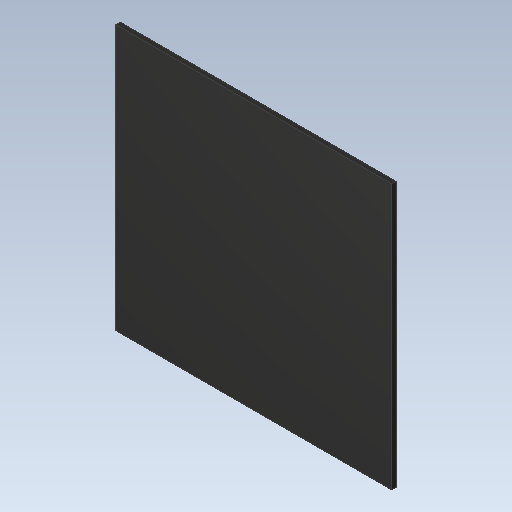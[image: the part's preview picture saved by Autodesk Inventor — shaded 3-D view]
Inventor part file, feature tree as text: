
AUTODESK INVENTOR PART (.ipt)
format: ipt  version: 2023 (Build 270158000, 158)  size: 92,672 bytes
history: imported  units: in
note: dims shown in document units (in); Inventor stores cm internally (conversion verified against a paired STEP export)
features: imported_body x1
ambient origin geometry x8: Origin, YZ Plane, XZ Plane, XY Plane, X Axis, Y Axis, Z Axis, Center Point
bodies: Solid1 (imported_parasolid), Body1 (imported_parasolid)
feature tree (1):
  imported_body  NMx_Import_Brep_tag  [imported B-rep: ~6 faces, bbox_mm=[6.35, 6.1, 0.1]]
